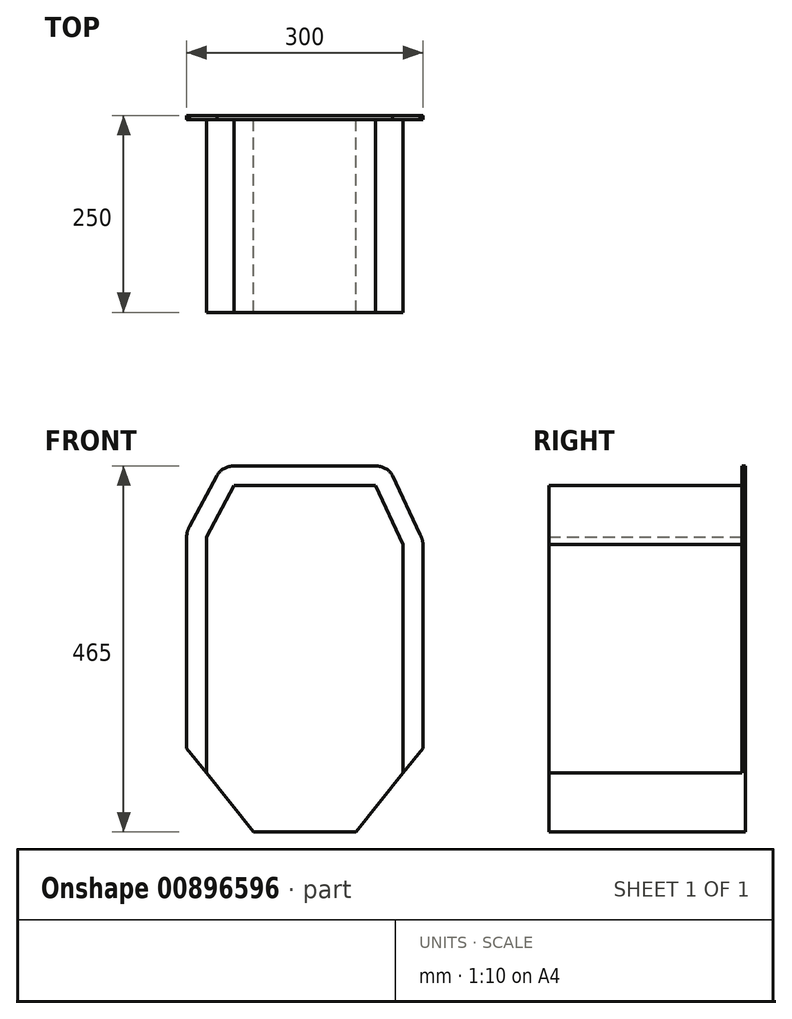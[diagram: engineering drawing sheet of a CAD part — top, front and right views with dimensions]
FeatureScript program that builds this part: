
annotation { "Feature Type Name" : "Feature", "Feature Type Description" : "" }
export const myFeature = defineFeature(function(context is Context, id is Id, definition is map)
    precondition{}
    {
        {
            var Q0;
            Q0=qCreatedBy(makeId("Front.planeOp"),FACE);
            var sketch = newSketch(context, id + "F0", { "sketchPlane" : qUnion([Q0])});
            skLineSegment(sketch, "E0", {"start": v(0, 220) * mm, "end": v(-125, 220) * mm, "construction": true});
            skPoint(sketch, "E1", {"position": v(0, 220) * mm});
            skLineSegment(sketch, "E2", {"start": v(0, 220) * mm, "end": v(0, -220) * mm, "construction": true});
            skLineSegment(sketch, "E3", {"start": v(0, -220) * mm, "end": v(125, -220) * mm, "construction": true});
            skLineSegment(sketch, "E4", {"start": v(0, 220) * mm, "end": v(125, 220) * mm, "construction": true});
            skLineSegment(sketch, "E5", {"start": v(-125, 220) * mm, "end": v(-125, -220) * mm, "construction": true});
            skLineSegment(sketch, "E6", {"start": v(125, 220) * mm, "end": v(125, -220) * mm, "construction": true});
            skLineSegment(sketch, "E7", {"start": v(-125, 220) * mm, "end": v(-90, 220) * mm, "construction": true});
            skLineSegment(sketch, "E8", {"start": v(125, 220) * mm, "end": v(90, 220) * mm, "construction": true});
            skLineSegment(sketch, "E9", {"start": v(0, -220) * mm, "end": v(-125, -220) * mm, "construction": true});
            skLineSegment(sketch, "E10", {"start": v(-125, -220) * mm, "end": v(-65, -220) * mm, "construction": true});
            skLineSegment(sketch, "E11", {"start": v(125, -220) * mm, "end": v(65, -220) * mm, "construction": true});
            skLineSegment(sketch, "E12", {"start": v(-125, -220) * mm, "end": v(-125, -120) * mm, "construction": true});
            skLineSegment(sketch, "E13", {"start": v(-125, -120) * mm, "end": v(-125, -79) * mm, "construction": true});
            skLineSegment(sketch, "E14", {"start": v(-125, 220) * mm, "end": v(-125, 121.5) * mm, "construction": true});
            skLineSegment(sketch, "E15", {"start": v(-125, 121.5) * mm, "end": v(-125, 80.5) * mm, "construction": true});
            skLineSegment(sketch, "E16", {"start": v(-125, 121.5) * mm, "end": v(125, 121.5) * mm, "construction": true});
            skLineSegment(sketch, "E17", {"start": v(-125, 80.5) * mm, "end": v(125, 80.5) * mm, "construction": true});
            skLineSegment(sketch, "E18", {"start": v(-125, -79) * mm, "end": v(125, -79) * mm, "construction": true});
            skLineSegment(sketch, "E19", {"start": v(-125, -120) * mm, "end": v(125, -120) * mm, "construction": true});
            skLineSegment(sketch, "E20", {"start": v(-125, -120) * mm, "end": v(-120, -120) * mm, "construction": true});
            skLineSegment(sketch, "E21", {"start": v(125, -120) * mm, "end": v(120, -120) * mm, "construction": true});
            skLineSegment(sketch, "E22", {"start": v(-120, 121.5) * mm, "end": v(-120, 80.5) * mm, "construction": true});
            skLineSegment(sketch, "E23", {"start": v(-120, -120) * mm, "end": v(-120, -79) * mm, "construction": true});
            skLineSegment(sketch, "E24", {"start": v(120, -120) * mm, "end": v(120, -79) * mm, "construction": true});
            skLineSegment(sketch, "E25", {"start": v(120, 121.5) * mm, "end": v(120, 80.5) * mm, "construction": true});
            skLineSegment(sketch, "E26", {"start": v(-125, -220) * mm, "end": v(-125, -145) * mm, "construction": true});
            skLineSegment(sketch, "E27", {"start": v(125, -220) * mm, "end": v(125, -145) * mm, "construction": true});
            skLineSegment(sketch, "E28", {"start": v(-65, -220) * mm, "end": v(-125, -145) * mm, "construction": true});
            skLineSegment(sketch, "E29", {"start": v(65, -220) * mm, "end": v(125, -145) * mm, "construction": true});
            skLineSegment(sketch, "E30", {"start": v(-125, 220) * mm, "end": v(-125, 155) * mm, "construction": true});
            skLineSegment(sketch, "E31", {"start": v(125, 220) * mm, "end": v(125, 145) * mm, "construction": true});
            skLineSegment(sketch, "E32", {"start": v(-125, 155) * mm, "end": v(-90, 220) * mm});
            skLineSegment(sketch, "E33", {"start": v(-90, 220) * mm, "end": v(90, 220) * mm});
            skLineSegment(sketch, "E34", {"start": v(90, 220) * mm, "end": v(125, 145) * mm});
            skLineSegment(sketch, "E35", {"start": v(125, 145) * mm, "end": v(125, -145) * mm});
            skLineSegment(sketch, "E36", {"start": v(125, -145) * mm, "end": v(65, -220) * mm});
            skLineSegment(sketch, "E37", {"start": v(65, -220) * mm, "end": v(-65, -220) * mm});
            skLineSegment(sketch, "E38", {"start": v(-65, -220) * mm, "end": v(-125, -145) * mm});
            skLineSegment(sketch, "E39", {"start": v(-125, -145) * mm, "end": v(-125, 155) * mm});
            skLineSegment(sketch, "E40", {"start": v(-125, -145) * mm, "end": v(-150, -145) * mm, "construction": true});
            skLineSegment(sketch, "E41", {"start": v(-125, 155) * mm, "end": v(-150, 155) * mm, "construction": true});
            skLineSegment(sketch, "E42", {"start": v(-150, 155) * mm, "end": v(-150, -145) * mm, "construction": true});
            skLineSegment(sketch, "E43", {"start": v(125, -145) * mm, "end": v(150, -145) * mm, "construction": true});
            skLineSegment(sketch, "E44", {"start": v(125, 145) * mm, "end": v(150, 145) * mm, "construction": true});
            skLineSegment(sketch, "E45", {"start": v(150, 145) * mm, "end": v(150, -145) * mm, "construction": true});
            skLineSegment(sketch, "E46", {"start": v(-65, -220) * mm, "end": v(-150, -113.75) * mm, "construction": true});
            skLineSegment(sketch, "E47", {"start": v(65, -220) * mm, "end": v(150, -113.75) * mm, "construction": true});
            skLineSegment(sketch, "E48", {"start": v(-90, 220) * mm, "end": v(-90, 245) * mm, "construction": true});
            skLineSegment(sketch, "E49", {"start": v(90, 220) * mm, "end": v(90, 245) * mm, "construction": true});
            skLineSegment(sketch, "E50", {"start": v(-90, 245) * mm, "end": v(90, 245) * mm, "construction": true});
            skPoint(sketch, "E51", {"position": v(-146.3, 168.1) * mm});
            skPoint(sketch, "E52", {"position": v(-111.3, 233.1) * mm});
            skPoint(sketch, "E53", {"position": v(146.3, 158.1) * mm});
            skPoint(sketch, "E54", {"position": v(111.3, 233.1) * mm});
            skArc(sketch, "E55", {"start": v(90, 245) * mm, "mid": v(102.2, 241.82) * mm, "end": v(111.3, 233.1) * mm});
            skArc(sketch, "E56", {"start": v(150, 145) * mm, "mid": v(149.06, 151.8) * mm, "end": v(146.3, 158.1) * mm});
            skLineSegment(sketch, "E57", {"start": v(111.3, 233.1) * mm, "end": v(146.3, 158.1) * mm});
            skArc(sketch, "E58", {"start": v(-90, 245) * mm, "mid": v(-102.2, 241.82) * mm, "end": v(-111.3, 233.1) * mm});
            skArc(sketch, "E59", {"start": v(-150, 155) * mm, "mid": v(-149.06, 161.8) * mm, "end": v(-146.3, 168.1) * mm});
            skLineSegment(sketch, "E60", {"start": v(-146.3, 168.1) * mm, "end": v(-111.3, 233.1) * mm});
            skLineSegment(sketch, "E61", {"start": v(-90, 245) * mm, "end": v(90, 245) * mm});
            skLineSegment(sketch, "E62", {"start": v(-150, 155) * mm, "end": v(-150, -113.75) * mm});
            skLineSegment(sketch, "E63", {"start": v(-150, -113.75) * mm, "end": v(-125, -145) * mm});
            skLineSegment(sketch, "E64", {"start": v(125, -145) * mm, "end": v(150, -113.75) * mm});
            skLineSegment(sketch, "E65", {"start": v(150, -113.75) * mm, "end": v(150, 145) * mm});
            skPoint(sketch, "E66", {"position": v(137.5, 145) * mm});
            skLineSegment(sketch, "E67", {"start": v(137.5, 145) * mm, "end": v(137.5, -129.37) * mm, "construction": true});
            skPoint(sketch, "E68", {"position": v(-137.5, 155) * mm});
            skLineSegment(sketch, "E69", {"start": v(-137.5, 155) * mm, "end": v(-137.5, -129.37) * mm, "construction": true});
            skPoint(sketch, "E70", {"position": v(90, 232.5) * mm});
            skPoint(sketch, "E71", {"position": v(-90, 232.5) * mm});
            skLineSegment(sketch, "E72", {"start": v(90, 232.5) * mm, "end": v(-90, 232.5) * mm, "construction": true});
            skLineSegment(sketch, "E73", {"start": v(146.3, 158.1) * mm, "end": v(125, 145) * mm, "construction": true});
            skLineSegment(sketch, "E74", {"start": v(-125, 155) * mm, "end": v(-146.3, 168.1) * mm, "construction": true});
            skLineSegment(sketch, "E75", {"start": v(-90, 220) * mm, "end": v(-111.3, 233.1) * mm, "construction": true});
            skLineSegment(sketch, "E76", {"start": v(90, 220) * mm, "end": v(111.3, 233.1) * mm, "construction": true});
            skPoint(sketch, "E77", {"position": v(100.65, 226.55) * mm});
            skPoint(sketch, "E78", {"position": v(135.65, 151.55) * mm});
            skPoint(sketch, "E79", {"position": v(-135.65, 161.55) * mm});
            skPoint(sketch, "E80", {"position": v(-100.65, 226.55) * mm});
            skArc(sketch, "E81", {"start": v(90, 232.5) * mm, "mid": v(96.1, 230.91) * mm, "end": v(100.65, 226.55) * mm, "construction": true});
            skArc(sketch, "E82", {"start": v(137.5, 145) * mm, "mid": v(137.03, 148.4) * mm, "end": v(135.65, 151.55) * mm, "construction": true});
            skArc(sketch, "E83", {"start": v(-135.65, 161.55) * mm, "mid": v(-137.03, 158.4) * mm, "end": v(-137.5, 155) * mm, "construction": true});
            skArc(sketch, "E84", {"start": v(-100.65, 226.55) * mm, "mid": v(-96.1, 230.91) * mm, "end": v(-90, 232.5) * mm, "construction": true});
            skLineSegment(sketch, "E85", {"start": v(-100.65, 226.55) * mm, "end": v(-135.65, 161.55) * mm, "construction": true});
            skLineSegment(sketch, "E86", {"start": v(137.5, 145) * mm, "end": v(100.65, 226.55) * mm, "construction": true});
            skLineSegment(sketch, "E87", {"start": v(125, 121.5) * mm, "end": v(150, 121.5) * mm, "construction": true});
            skLineSegment(sketch, "E88", {"start": v(150, 121.5) * mm, "end": v(125, 80.5) * mm, "construction": true});
            skLineSegment(sketch, "E89", {"start": v(125, 80.5) * mm, "end": v(150, 80.5) * mm, "construction": true});
            skLineSegment(sketch, "E90", {"start": v(-125, 80.5) * mm, "end": v(-150, 80.5) * mm, "construction": true});
            skLineSegment(sketch, "E91", {"start": v(-150, 80.5) * mm, "end": v(-125, 121.5) * mm, "construction": true});
            skLineSegment(sketch, "E92", {"start": v(-125, 121.5) * mm, "end": v(-150, 121.5) * mm, "construction": true});
            skPoint(sketch, "E93", {"position": v(137.5, 101) * mm});
            skPoint(sketch, "E94", {"position": v(-137.5, 101) * mm});
            skLineSegment(sketch, "E95", {"start": v(125, -120) * mm, "end": v(150, -120) * mm, "construction": true});
            skLineSegment(sketch, "E96", {"start": v(125, -79) * mm, "end": v(150, -79) * mm, "construction": true});
            skLineSegment(sketch, "E97", {"start": v(-125, -120) * mm, "end": v(-150, -120) * mm, "construction": true});
            skLineSegment(sketch, "E98", {"start": v(-125, -79) * mm, "end": v(-150, -79) * mm, "construction": true});
            skSolve(sketch);
        }
        {
            var Q0;
            Q0=makeQuery(id+"F0.imprint","IMPRINT",FACE,{"disambiguationData":[TD([[makeQuery(id+"F0.imprint","IMPRINT",EDGE,{"derivedFrom":sQuery(id+"F0.wireOp",EDGE,"E32")}),-1.0]])]});
            extrude(context, id + "F1", {"entities" : qUnion([Q0]), "depth" : 250 * mm, "offsetDistance" : 25 * mm});
        }
        {
            var Q0;
            Q0=makeQuery(id+"F0.imprint","IMPRINT",FACE,{"disambiguationData":[TD([[makeQuery(id+"F0.imprint","IMPRINT",EDGE,{"derivedFrom":sQuery(id+"F0.wireOp",EDGE,"E32")}),1.0]])]});
            extrude(context, id + "F2", {"entities" : qUnion([Q0]), "operationType" : NewBodyOperationType.ADD, "depth" : 5 * mm, "offsetDistance" : 25 * mm});
        }
    });
